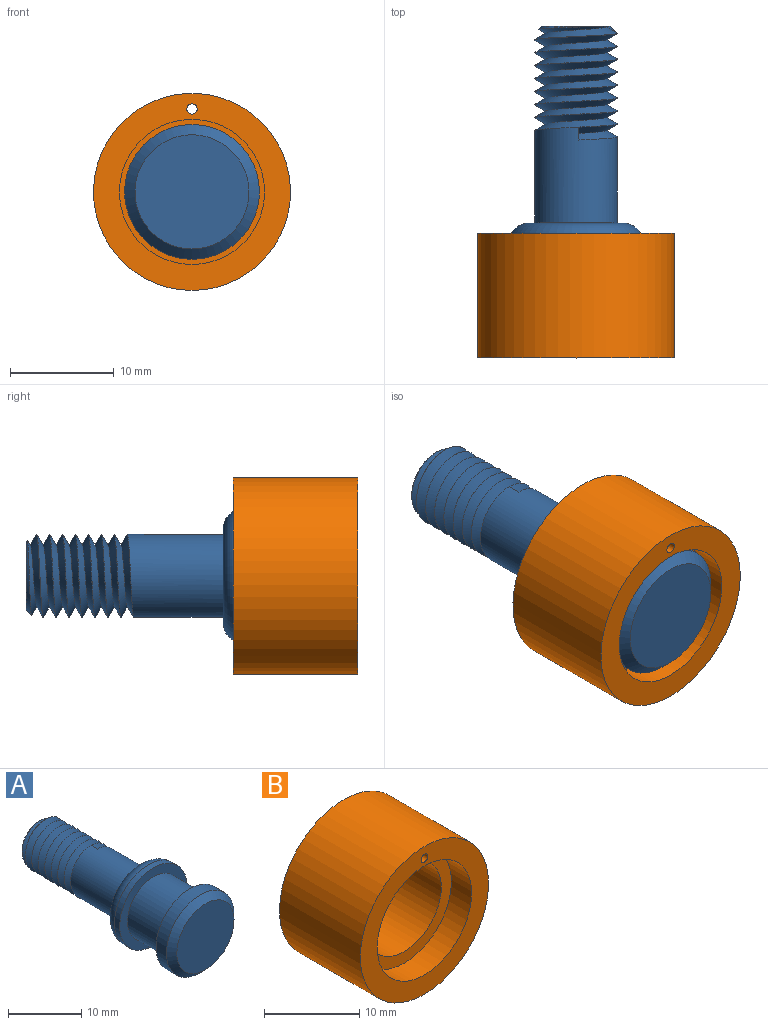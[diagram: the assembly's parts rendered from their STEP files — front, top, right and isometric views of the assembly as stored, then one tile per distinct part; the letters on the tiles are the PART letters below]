
ASSEMBLY  parts=2 mates=1
PART A: 23 faces, bbox 14.1x32.6x14.1 mm
  f0: cylinder r=4mm len=9.86mm, axis (0,-1,0), area 216.9mm2, adj f7,f8,f20,f21,f22
  f1: cylinder r=4mm len=8mm, axis (0,-1,0), area 0.2mm2, adj f2,f18,f21,f22
  f2: cylinder r=4mm len=8mm, axis (0,-1,0), area 0.3mm2, adj f1,f3,f21,f22
  f3: cylinder r=4mm len=8mm, axis (0,-1,0), area 0.2mm2, adj f2,f4,f21,f22
  f4: cylinder r=4mm len=8mm, axis (0,-1,0), area 0.2mm2, adj f3,f5,f21,f22
  f5: cylinder r=4mm len=8mm, axis (0,-1,0), area 0.3mm2, adj f4,f6,f21,f22
  f6: cylinder r=4mm len=8mm, axis (0,-1,0), area 0.3mm2, adj f5,f7,f21,f22
  f7: cylinder r=4mm len=8mm, axis (0,-1,0), area 0.2mm2, adj f0,f6,f21,f22
  f8: plane 9x9mm, normal (0,1,0), area 13.4mm2, adj f0,f9
  f9: torus R=4.5mm, axis (0,-1,0), area 114mm2, adj f8,f10
  f10: cylinder r=6.5mm len=13mm, axis (0,-1,0), area 40.8mm2, adj f9,f11
  f11: plane 13x13mm, normal (0,-1,0), area 54.2mm2, adj f10,f12
  f12: cylinder r=5mm len=10mm, axis (0,-1,0), area 219.9mm2, adj f11,f13
  f13: plane 13x13mm, normal (0,1,0), area 54.2mm2, adj f12,f14
  f14: cylinder r=6.5mm len=13mm, axis (0,-1,0), area 81.7mm2, adj f13,f15
  f15: cone r=5.5mm half-angle=45deg, axis (0,1,0), area 53.3mm2, adj f14,f16
  f16: plane 11x11mm, normal (0,-1,0), area 95mm2, adj f15
  f17: plane 6.68x6.68mm, normal (0,1,0), area 34mm2, adj f18,f19,f21
  f18: cone r=4mm half-angle=45deg, axis (0,-1,0), area 9.9mm2, adj f1,f17,f19,f21
  f19: plane 1.07x0.7mm, normal (0,0,1), area 0.2mm2, adj f17,f18,f21,f22
  f20: plane 1.24x1.07mm, normal (1,0,-0.06), area 0.7mm2, adj f0,f21,f22
  f21: bspline ~11.04x9.24mm, area 211.8mm2, adj f0,f1,f2,f3,f4,f5,f6,f7
  f22: bspline ~11.04x9.24mm, area 222.6mm2, adj f0,f1,f2,f3,f4,f5,f6,f7
PART B: 9 faces, bbox 19x12x19 mm
  f0: cylinder r=9.5mm len=19mm, axis (0,-1,0), area 716.3mm2, adj f1,f7
  f1: plane 19x19mm, normal (0,-1,0), area 128.8mm2, adj f0,f2,f8
  f2: cylinder r=7mm len=14mm, axis (0,-1,0), area 131.9mm2, adj f1,f3
  f3: plane 14x14mm, normal (0,-1,0), area 58.9mm2, adj f2,f4
  f4: cylinder r=5.5mm len=11mm, axis (0,-1,0), area 207.3mm2, adj f3,f5
  f5: plane 14x14mm, normal (0,1,0), area 58.9mm2, adj f4,f6
  f6: cylinder r=7mm len=14mm, axis (0,-1,0), area 131.9mm2, adj f5,f7
  f7: plane 19x19mm, normal (0,1,0), area 128.8mm2, adj f0,f6,f8
  f8: cylinder r=0.5mm len=12mm, axis (0,-1,0), area 37.7mm2, adj f1,f7
PLACE A at identity fixed
PLACE B t=(0,-0.5,0)mm
MATE revolute B.f0 <-> A.f0  axis (0,-1,0) through (0,0,0)mm
